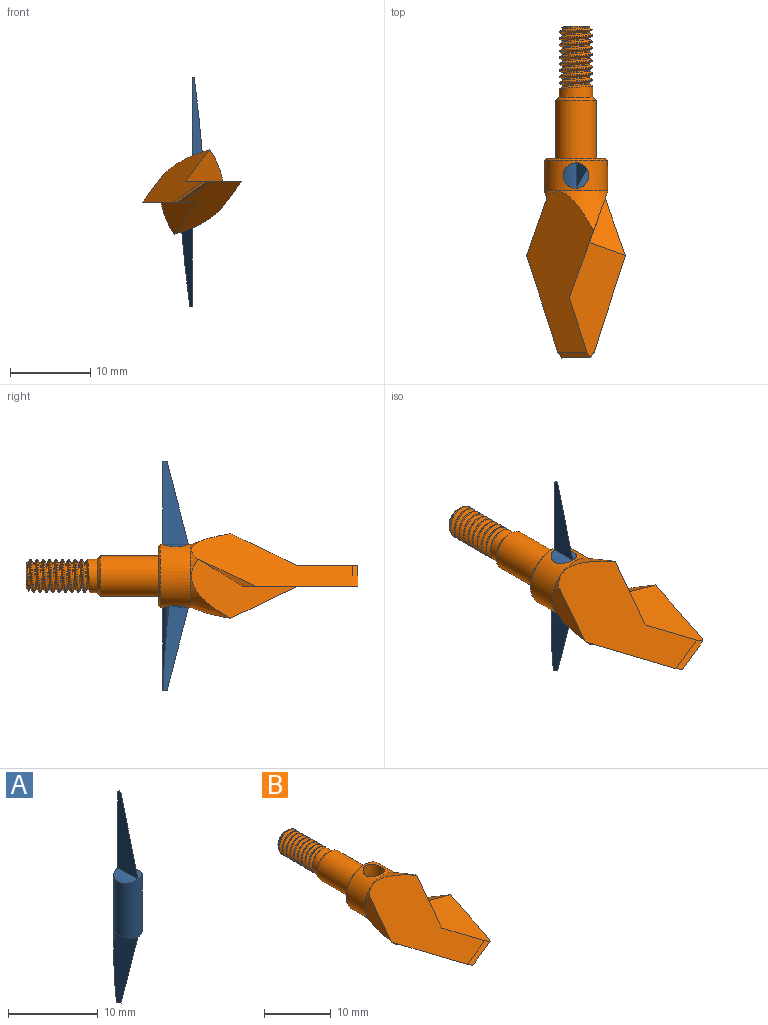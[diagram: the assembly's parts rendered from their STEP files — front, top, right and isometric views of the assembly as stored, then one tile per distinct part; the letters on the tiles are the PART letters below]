
ASSEMBLY  parts=2 mates=1
PART A: 11 faces, bbox 3.2x3.2x28.6 mm
  f0: cylinder r=1.59mm len=28.58mm, axis (0,0,-1), area 94.9mm2, adj f1,f2,f3,f4,f5,f6,f7,f8
  f1: plane 0.51x0.27mm, normal (0,0,-1), area 0.1mm2, adj f0,f6,f9
  f2: plane 0.51x0.27mm, normal (0,0,1), area 0.1mm2, adj f0,f4,f7
  f3: cylinder r=3.94mm len=3.18mm, axis (0,1,0), area 4mm2, adj f0,f4
  f4: plane 10.35x3.18mm, normal (-1,0,0), area 19.1mm2, adj f0,f2,f3,f7
  f5: cylinder r=3.94mm len=3.18mm, axis (0,1,0), area 4mm2, adj f0,f6
  f6: plane 10.35x3.18mm, normal (1,0,0), area 19.1mm2, adj f0,f1,f5,f9
  f7: plane 10.66x3.22mm, normal (0.87,-0.48,0.12), area 18.6mm2, adj f0,f2,f4,f8
  f8: cylinder r=3.94mm len=2.39mm, axis (0,1,0), area 1.6mm2, adj f0,f7
  f9: plane 10.67x3.22mm, normal (-0.87,-0.48,-0.12), area 18.6mm2, adj f0,f1,f6,f10
  f10: cylinder r=3.94mm len=2.39mm, axis (0,1,0), area 1.6mm2, adj f0,f9
PART B: 34 faces, bbox 12.7x42x11.8 mm
  f0: cylinder r=2.08mm len=4.17mm, axis (0,-1,0), area 14.6mm2, adj f1,f12,f14,f15,f17
  f1: cylinder r=2.08mm len=4.17mm, axis (0,-1,0), area 1.4mm2, adj f0,f2,f14,f15
  f2: cylinder r=2.08mm len=4.17mm, axis (0,-1,0), area 1.4mm2, adj f1,f3,f14,f15
  f3: cylinder r=2.08mm len=4.17mm, axis (0,-1,0), area 1.4mm2, adj f2,f4,f14,f15
  f4: cylinder r=2.08mm len=4.17mm, axis (0,-1,0), area 1.4mm2, adj f3,f5,f14,f15
  f5: cylinder r=2.08mm len=4.17mm, axis (0,-1,0), area 1.4mm2, adj f4,f6,f14,f15
  f6: cylinder r=2.08mm len=4.17mm, axis (0,-1,0), area 1.4mm2, adj f5,f7,f14,f15
  f7: cylinder r=2.08mm len=4.17mm, axis (0,-1,0), area 1.4mm2, adj f6,f8,f14,f15
  f8: cylinder r=2.08mm len=4.17mm, axis (0,-1,0), area 1.4mm2, adj f7,f9,f14,f15
  f9: cylinder r=2.08mm len=1.58mm, axis (0,-1,0), area 0.1mm2, adj f8,f11,f14
  f10: plane 3.15x3.15mm, normal (0,1,0), area 7.8mm2, adj f11
  f11: cone r=1.57mm half-angle=45deg, axis (0,-1,0), area 4.2mm2, adj f9,f10,f13,f14,f15
  f12: plane 0.69x0.44mm, normal (0,0,-1), area 0.2mm2, adj f0,f13,f14,f15
  f13: cylinder r=1.65mm len=7.93mm, axis (0,1,0), area 18.7mm2, adj f11,f12,f14,f15
  f14: bspline ~8.06x4.81mm, area 54.9mm2, adj f0,f1,f2,f3,f4,f5,f6,f7
  f15: bspline ~8.19x4.81mm, area 58.2mm2, adj f0,f1,f2,f3,f4,f5,f6,f7
  f16: cylinder r=2.54mm len=7.24mm, axis (0,-1,0), area 115.5mm2, adj f18,f20
  f17: plane 4.32x4.32mm, normal (0,1,0), area 1mm2, adj f0,f18
  f18: cone r=2.54mm half-angle=45deg, axis (0,-1,0), area 8mm2, adj f16,f17
  f19: cylinder r=3.94mm len=7.87mm, axis (0,1,0), area 78.1mm2, adj f21,f22,f23
  f20: plane 7.37x7.37mm, normal (0,1,0), area 22.3mm2, adj f16,f22
  f21: cylinder r=1.59mm len=7.87mm, axis (0,0,1), area 75.2mm2, adj f19
  f22: cone r=3.94mm half-angle=45deg, axis (0,-1,0), area 8.6mm2, adj f19,f20
  f23: cone r=6.06mm half-angle=19.6deg, axis (0,-1,0), area 35mm2, adj f19,f30,f31,f32,f33
  f24: plane 4.07x2.54mm, normal (0.54,-0.34,-0.77), area 3.3mm2, adj f25,f27,f29,f33
  f25: plane 4.07x2.54mm, normal (-0.54,-0.34,0.77), area 3.3mm2, adj f24,f27,f29,f32
  f26: plane 7.11x4.5mm, normal (0.17,0.47,0.87), area 16.1mm2, adj f27,f30,f33
  f27: plane 14.4x7mm, normal (0,0,1), area 52.8mm2, adj f24,f25,f26,f30,f32,f33
  f28: plane 7.11x4.5mm, normal (-0.17,0.47,-0.87), area 16.1mm2, adj f29,f31,f32
  f29: plane 14.4x7mm, normal (0,0,-1), area 52.8mm2, adj f24,f25,f28,f31,f32,f33
  f30: plane 13.21x7.37mm, normal (0.94,-0.34,0), area 41.8mm2, adj f23,f26,f27,f32,f33
  f31: plane 13.21x7.37mm, normal (-0.94,-0.34,0), area 41.8mm2, adj f23,f28,f29,f32,f33
  f32: plane 20.05x8.35mm, normal (-0.56,-0.18,0.81), area 122.6mm2, adj f23,f25,f27,f28,f29,f30,f31
  f33: plane 20.42x8.72mm, normal (0.56,-0.18,-0.81), area 122.6mm2, adj f23,f24,f26,f27,f29,f30,f31
PLACE A t=(0,-2.16,0)mm
PLACE B at identity fixed
MATE cylindrical B.f21 <-> A.f0  axis (0,0,1) through (0,-2.16,0)mm
